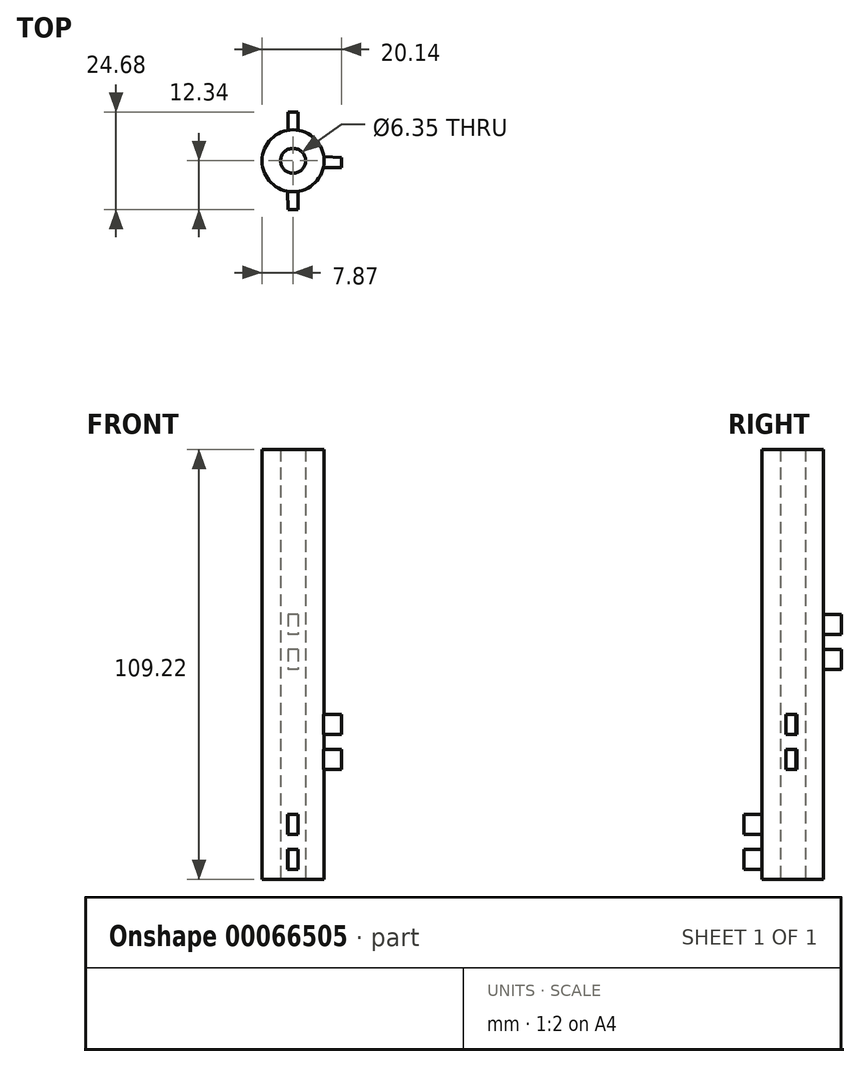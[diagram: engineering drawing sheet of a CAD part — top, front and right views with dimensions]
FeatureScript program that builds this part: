
annotation { "Feature Type Name" : "Feature", "Feature Type Description" : "" }
export const myFeature = defineFeature(function(context is Context, id is Id, definition is map)
    precondition{}
    {
        {
            var Q0;
            Q0=qCreatedBy(makeId("Top.planeOp"),FACE);
            var sketch = newSketch(context, id + "F0", { "sketchPlane" : qUnion([Q0])});
            skCircle(sketch, "E0", {"center": v(0, 0) * mm, "radius": 7.87 * mm});
            skCircle(sketch, "E1", {"center": v(0, 0) * mm, "radius": 3.18 * mm});
            skLineSegment(sketch, "E2.rect.left", {"start": v(12.27, 0.86) * mm, "end": v(12.27, -1.68) * mm});
            skLineSegment(sketch, "E3", {"start": v(7.8, 1.02) * mm, "end": v(12.27, 0.86) * mm});
            skLineSegment(sketch, "E4", {"start": v(12.27, -1.68) * mm, "end": v(7.7, -1.68) * mm});
            skLineSegment(sketch, "E5.rect.bottom", {"start": v(1.27, 12.34) * mm, "end": v(-1.27, 12.34) * mm});
            skLineSegment(sketch, "E5.rect.top", {"start": v(1.27, -12.34) * mm, "end": v(-1.27, -12.34) * mm});
            skLineSegment(sketch, "E6", {"start": v(-1.43, -7.74) * mm, "end": v(-1.27, -12.34) * mm});
            skLineSegment(sketch, "E7", {"start": v(1.27, -12.34) * mm, "end": v(1.27, -7.77) * mm});
            skLineSegment(sketch, "E8", {"start": v(-1.27, 12.34) * mm, "end": v(-1.27, 7.77) * mm});
            skLineSegment(sketch, "E9", {"start": v(1.27, 12.34) * mm, "end": v(1.27, 7.77) * mm});
            skLineSegment(sketch, "E10", {"start": v(2.73, -7.77) * mm, "end": v(-5.06, -7.77) * mm, "construction": true});
            skSolve(sketch);
        }
        {
            var Q0;
            Q0=makeQuery(id+"F0.imprint","IMPRINT",FACE,{"disambiguationData":[TD([[makeQuery(id+"F0.imprint","IMPRINT",EDGE,{"derivedFrom":sQuery(id+"F0.wireOp",EDGE,"E0")}),1.0]])]});
            extrude(context, id + "F1", {"entities" : qUnion([Q0]), "depth" : 127 * mm});
        }
        {
            var Q0;
            Q0=makeQuery(id+"F0.imprint","IMPRINT",FACE,{"disambiguationData":[TD([[makeQuery(id+"F0.imprint","IMPRINT",EDGE,{"derivedFrom":sQuery(id+"F0.wireOp",EDGE,"E5.rect.bottom")}),1.0]])]});
            extrude(context, id + "F2", {"entities" : qUnion([Q0]), "operationType" : NewBodyOperationType.ADD, "depth" : 76.2 * mm});
        }
        {
            var Q0;
            Q0=makeQuery(id+"F0.imprint","IMPRINT",FACE,{"disambiguationData":[TD([[makeQuery(id+"F0.imprint","IMPRINT",EDGE,{"derivedFrom":sQuery(id+"F0.wireOp",EDGE,"E5.rect.bottom")}),1.0]])]});
            extrude(context, id + "F3", {"entities" : qUnion([Q0]), "operationType" : NewBodyOperationType.REMOVE, "depth" : 71.12 * mm});
        }
        {
            var Q0;
            Q0=makeQuery(id+"F0.imprint","IMPRINT",FACE,{"disambiguationData":[TD([[makeQuery(id+"F0.imprint","IMPRINT",EDGE,{"derivedFrom":sQuery(id+"F0.wireOp",EDGE,"E2.rect.left")}),-1.0]])]});
            extrude(context, id + "F4", {"entities" : qUnion([Q0]), "operationType" : NewBodyOperationType.ADD, "depth" : 50.8 * mm});
        }
        {
            var Q0;
            Q0=makeQuery(id+"F0.imprint","IMPRINT",FACE,{"disambiguationData":[TD([[makeQuery(id+"F0.imprint","IMPRINT",EDGE,{"derivedFrom":sQuery(id+"F0.wireOp",EDGE,"E2.rect.left")}),-1.0]])]});
            extrude(context, id + "F5", {"entities" : qUnion([Q0]), "operationType" : NewBodyOperationType.REMOVE, "depth" : 45.72 * mm});
        }
        {
            var Q0;
            Q0=makeQuery(id+"F0.imprint","IMPRINT",FACE,{"disambiguationData":[TD([[makeQuery(id+"F0.imprint","IMPRINT",EDGE,{"derivedFrom":sQuery(id+"F0.wireOp",EDGE,"E5.rect.top")}),-1.0]])]});
            extrude(context, id + "F6", {"entities" : qUnion([Q0]), "operationType" : NewBodyOperationType.ADD, "depth" : 25.4 * mm});
        }
        {
            var Q0;
            Q0=makeQuery(id+"F0.imprint","IMPRINT",FACE,{"disambiguationData":[TD([[makeQuery(id+"F0.imprint","IMPRINT",EDGE,{"derivedFrom":sQuery(id+"F0.wireOp",EDGE,"E5.rect.top")}),-1.0]])]});
            extrude(context, id + "F7", {"entities" : qUnion([Q0]), "operationType" : NewBodyOperationType.REMOVE, "depth" : 20.32 * mm});
        }
        {
            var Q0;
            Q0=makeQuery(id+"F2.opExtrude","CAP_FACE",FACE,{"disambiguationData":[OSD([sQuery(id+"F0.wireOp",EDGE,"E0"),sQuery(id+"F0.wireOp",EDGE,"E5.rect.bottom"),sQuery(id+"F0.wireOp",EDGE,"E8"),sQuery(id+"F0.wireOp",EDGE,"E9")])],"isStart":false});
            var sketch = newSketch(context, id + "F8", { "sketchPlane" : qUnion([Q0])});
            skSolve(sketch);
        }
        {
            var Q0;
            Q0=makeQuery(id+"F8.imprint","IMPRINT",FACE,{"disambiguationData":[TD([[makeQuery(id+"F8.imprint","IMPRINT",EDGE,{"derivedFrom":makeQuery(id+"F2.opExtrude","CAP_EDGE",EDGE,{"disambiguationData":[OSD([sQuery(id+"F0.wireOp",EDGE,"E5.rect.bottom")])],"isStart":false})}),1.0]])]});
            extrude(context, id + "F9", {"entities" : qUnion([Q0]), "operationType" : NewBodyOperationType.ADD, "depth" : 8.9 * mm});
        }
        {
            var Q0;
            Q0=makeQuery(id+"F8.imprint","IMPRINT",FACE,{"disambiguationData":[TD([[makeQuery(id+"F8.imprint","IMPRINT",EDGE,{"derivedFrom":makeQuery(id+"F2.opExtrude","CAP_EDGE",EDGE,{"disambiguationData":[OSD([sQuery(id+"F0.wireOp",EDGE,"E5.rect.bottom")])],"isStart":false})}),1.0]])]});
            extrude(context, id + "F10", {"entities" : qUnion([Q0]), "operationType" : NewBodyOperationType.REMOVE, "depth" : 3.8 * mm});
        }
        {
            var Q0;
            Q0=makeQuery(id+"F4.opExtrude","CAP_FACE",FACE,{"disambiguationData":[OSD([sQuery(id+"F0.wireOp",EDGE,"E0"),sQuery(id+"F0.wireOp",EDGE,"E2.rect.left"),sQuery(id+"F0.wireOp",EDGE,"E3"),sQuery(id+"F0.wireOp",EDGE,"E4")])],"isStart":false});
            var sketch = newSketch(context, id + "F11", { "sketchPlane" : qUnion([Q0])});
            skSolve(sketch);
        }
        {
            var Q0;
            Q0 = qSketchRegion(id + "F11", true);
            var Q1;
            Q1=makeQuery(id+"F11.imprint","IMPRINT",FACE,{"disambiguationData":[TD([[makeQuery(id+"F11.imprint","IMPRINT",EDGE,{"derivedFrom":makeQuery(id+"F4.opExtrude","CAP_EDGE",EDGE,{"disambiguationData":[OSD([sQuery(id+"F0.wireOp",EDGE,"E2.rect.left")])],"isStart":false})}),-1.0]])]});
            extrude(context, id + "F12", {"entities" : qUnion([Q0, Q1]), "operationType" : NewBodyOperationType.ADD, "depth" : 8.9 * mm});
        }
        {
            var Q0;
            Q0=makeQuery(id+"F11.imprint","IMPRINT",FACE,{"disambiguationData":[TD([[makeQuery(id+"F11.imprint","IMPRINT",EDGE,{"derivedFrom":makeQuery(id+"F4.opExtrude","CAP_EDGE",EDGE,{"disambiguationData":[OSD([sQuery(id+"F0.wireOp",EDGE,"E2.rect.left")])],"isStart":false})}),-1.0]])]});
            extrude(context, id + "F13", {"entities" : qUnion([Q0]), "operationType" : NewBodyOperationType.REMOVE, "depth" : 3.8 * mm});
        }
        {
            var Q0;
            Q0=makeQuery(id+"F6.opExtrude","CAP_FACE",FACE,{"disambiguationData":[OSD([sQuery(id+"F0.wireOp",EDGE,"E0"),sQuery(id+"F0.wireOp",EDGE,"E5.rect.top"),sQuery(id+"F0.wireOp",EDGE,"E6"),sQuery(id+"F0.wireOp",EDGE,"E7")])],"isStart":false});
            var sketch = newSketch(context, id + "F14", { "sketchPlane" : qUnion([Q0])});
            skSolve(sketch);
        }
        {
            var Q0;
            Q0=makeQuery(id+"F14.imprint","IMPRINT",FACE,{"disambiguationData":[TD([[makeQuery(id+"F14.imprint","IMPRINT",EDGE,{"derivedFrom":makeQuery(id+"F6.opExtrude","CAP_EDGE",EDGE,{"disambiguationData":[OSD([sQuery(id+"F0.wireOp",EDGE,"E5.rect.top")])],"isStart":false})}),-1.0]])]});
            extrude(context, id + "F15", {"entities" : qUnion([Q0]), "operationType" : NewBodyOperationType.ADD, "depth" : 8.9 * mm});
        }
        {
            var Q0;
            Q0=makeQuery(id+"F14.imprint","IMPRINT",FACE,{"disambiguationData":[TD([[makeQuery(id+"F14.imprint","IMPRINT",EDGE,{"derivedFrom":makeQuery(id+"F6.opExtrude","CAP_EDGE",EDGE,{"disambiguationData":[OSD([sQuery(id+"F0.wireOp",EDGE,"E5.rect.top")])],"isStart":false})}),-1.0]])]});
            extrude(context, id + "F16", {"entities" : qUnion([Q0]), "operationType" : NewBodyOperationType.REMOVE, "depth" : 3.8 * mm});
        }
        {
            var Q0;
            Q0=makeQuery(id+"F0.imprint","IMPRINT",FACE,{"disambiguationData":[TD([[makeQuery(id+"F0.imprint","IMPRINT",EDGE,{"derivedFrom":sQuery(id+"F0.wireOp",EDGE,"E1")}),-1.0]])]});
            extrude(context, id + "F17", {"entities" : qUnion([Q0]), "operationType" : NewBodyOperationType.REMOVE, "depth" : 17.78 * mm});
        }
    });
